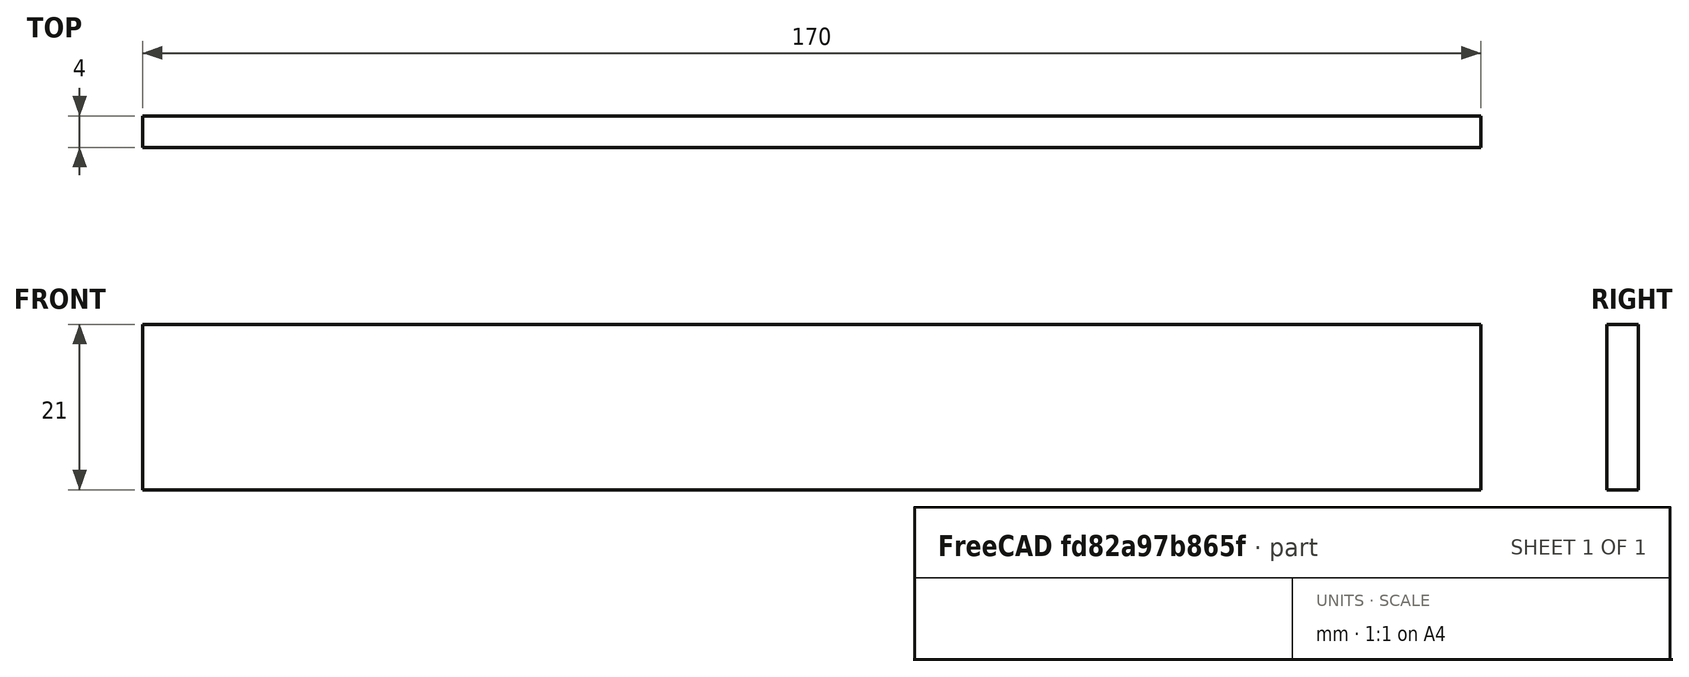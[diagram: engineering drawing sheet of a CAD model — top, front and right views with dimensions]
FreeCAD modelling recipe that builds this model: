
FCSTD DOCUMENT  (FreeCAD 0.17R13528 (Git))
Label: small_glass
License: All rights reserved
LicenseURL: http://en.wikipedia.org/wiki/All_rights_reserved
objects: Sketcher::SketchObject×1, PartDesign::Pad×1, PartDesign::Body×1
note: 4 computed .brp shape members not serialized (recipe doc carries the construction recipe); baked Part::Feature solids carry a one-line shape summary decoded from their .brp

FEATURE [Sketcher::SketchObject] Sketch
  MapMode = 5
  Placement = pos=(0,0,0) rot=(1,0,0;1.5708rad)
  Support = -> [XZ_Plane]
  sketch-geometry (4):
    g0: LineSegment StartX=0 StartY=0 StartZ=0 EndX=-170 EndY=0 EndZ=0
    g1: LineSegment StartX=-170 StartY=0 StartZ=0 EndX=-170 EndY=21 EndZ=0
    g2: LineSegment StartX=-170 StartY=21 StartZ=0 EndX=0 EndY=21 EndZ=0
    g3: LineSegment StartX=0 StartY=21 StartZ=0 EndX=0 EndY=0 EndZ=0
  constraints (11):
    c: Coincident(g0,g1)
    c: Coincident(g1,g2)
    c: Coincident(g2,g3)
    c: Coincident(g3,g0)
    c: Horizontal(g0)
    c: Horizontal(g2)
    c: Vertical(g1)
    c: Vertical(g3)
    c: Coincident(g0,g-1)
    c: DistanceY(g3,g3) = 21
    c: DistanceX(g0,g0) = 170
FEATURE [PartDesign::Pad] Pad
  Length = 4
  Length2 = 100
  Placement = pos=(0,0,0) rot=(1,0,0;1.5708rad)
  Profile = -> Sketch
  Type = 0
FEATURE [PartDesign::Body] Body
  Group = -> [Sketch,Pad]
  Origin = -> Origin
  Tip = -> Pad
